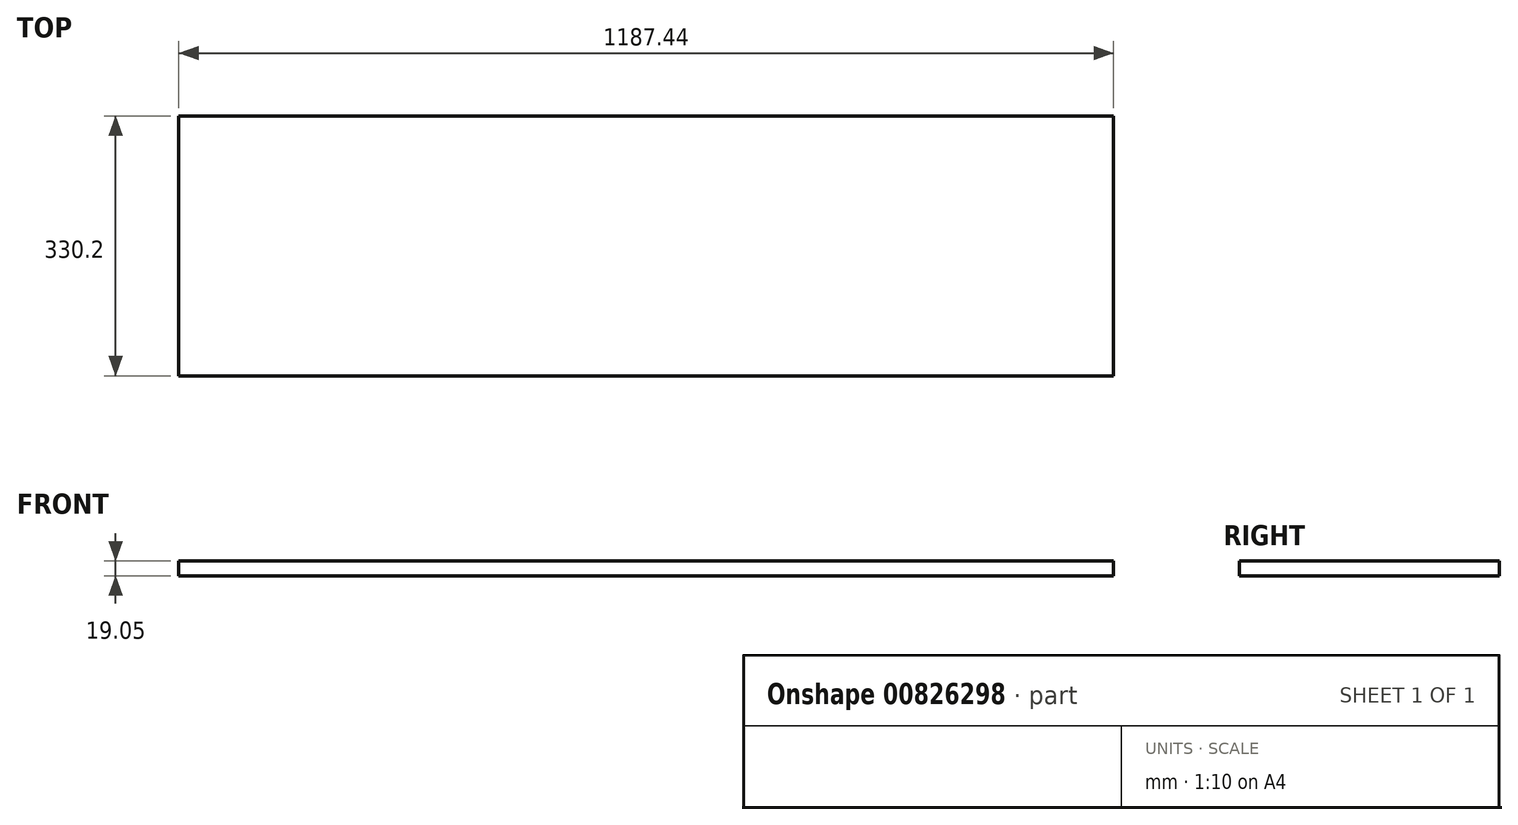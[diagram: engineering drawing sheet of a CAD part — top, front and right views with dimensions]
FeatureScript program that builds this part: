
annotation { "Feature Type Name" : "Feature", "Feature Type Description" : "" }
export const myFeature = defineFeature(function(context is Context, id is Id, definition is map)
    precondition{}
    {
        {
            var Q0;
            Q0=qCreatedBy(makeId("Top.planeOp"),FACE);
            var sketch = newSketch(context, id + "F0", { "sketchPlane" : qUnion([Q0])});
            skLineSegment(sketch, "E0.bottom", {"start": v(-593.73, -165.1) * mm, "end": v(593.73, -165.1) * mm});
            skLineSegment(sketch, "E0.top", {"start": v(-593.73, 165.1) * mm, "end": v(593.73, 165.1) * mm});
            skLineSegment(sketch, "E0.left", {"start": v(-593.73, -165.1) * mm, "end": v(-593.73, 165.1) * mm});
            skLineSegment(sketch, "E0.right", {"start": v(593.73, -165.1) * mm, "end": v(593.73, 165.1) * mm});
            skPoint(sketch, "E0.middle", {"position": v(0, 0) * mm});
            skSolve(sketch);
        }
        {
            var Q0;
            Q0 = qSketchRegion(id + "F0", true);
            extrude(context, id + "F1", {"entities" : qUnion([Q0]), "depth" : 19.05 * mm, "offsetDistance" : 25.4 * mm});
        }
        {
            var Q0;
            Q0=makeQuery(id+"F0.imprint","IMPRINT",FACE,{"disambiguationData":[TD([[makeQuery(id+"F0.imprint","IMPRINT",EDGE,{"derivedFrom":sQuery(id+"F0.wireOp",EDGE,"E0.bottom")}),1.0]])]});
            cPlane(context, id + "F2", {"entities" : qUnion([Q0]), "cplaneType" : CPlaneType.OFFSET, "offset" : 254 * mm, "oppositeDirection" : true, "width" : 152.4 * mm, "height" : 152.4 * mm});
        }
    });
